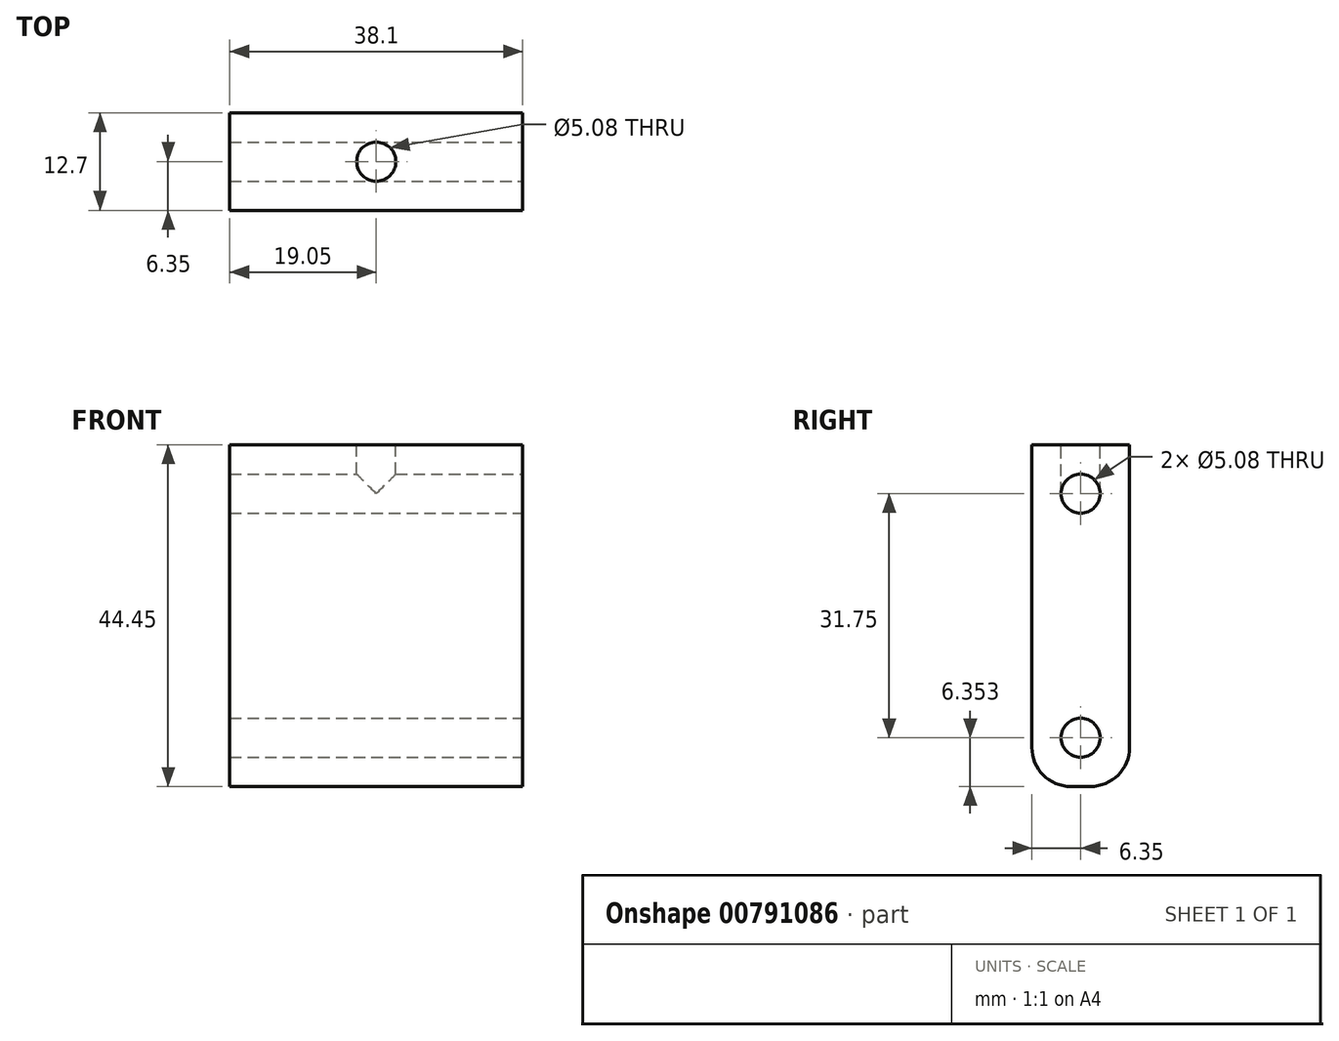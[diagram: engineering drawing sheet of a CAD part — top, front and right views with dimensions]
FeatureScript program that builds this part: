
annotation { "Feature Type Name" : "Feature", "Feature Type Description" : "" }
export const myFeature = defineFeature(function(context is Context, id is Id, definition is map)
    precondition{}
    {
        {
            var Q0;
            Q0=qCreatedBy(makeId("Front.planeOp"),FACE);
            var sketch = newSketch(context, id + "F0", { "sketchPlane" : qUnion([Q0])});
            skLineSegment(sketch, "E0.bottom", {"start": v(-38.1, 27.55) * mm, "end": v(0, 27.55) * mm});
            skLineSegment(sketch, "E0.top", {"start": v(-38.1, -16.9) * mm, "end": v(0, -16.9) * mm});
            skLineSegment(sketch, "E0.left", {"start": v(-38.1, 27.55) * mm, "end": v(-38.1, -16.9) * mm});
            skLineSegment(sketch, "E0.right", {"start": v(0, 27.55) * mm, "end": v(0, -16.9) * mm});
            skSolve(sketch);
        }
        {
            var Q0;
            Q0=qSketchRegion(id+"F0",true);
            extrude(context, id + "F1", {"entities" : qUnion([Q0]), "depth" : 12.7 * mm, "offsetDistance" : 25.4 * mm});
        }
        {
            var Q0;
            Q0=makeQuery(id+"F1.opExtrude","CAP_EDGE",EDGE,{"disambiguationData":[OSD([sQuery(id+"F0.wireOp",EDGE,"E0.top")])],"isStart":true});
            var Q1;
            Q1=makeQuery(id+"F1.opExtrude","CAP_EDGE",EDGE,{"disambiguationData":[OSD([sQuery(id+"F0.wireOp",EDGE,"E0.top")])],"isStart":false});
            fillet(context, id + "F2", {"entities" : qUnion([Q0, Q1]), "radius" : 5.08 * mm, "tangentPropagation" : true, "allowEdgeOverflow" : false});
        }
        {
            var Q0;
            Q0=makeQuery(id+"F1.opExtrude","SWEPT_FACE",FACE,{"disambiguationData":[OSD([sQuery(id+"F0.wireOp",EDGE,"E0.right")])]});
            var sketch = newSketch(context, id + "F3", { "sketchPlane" : qUnion([Q0])});
            skCircle(sketch, "E1", {"center": v(-6.35, -10.55) * mm, "radius": 2.54 * mm});
            skCircle(sketch, "E2", {"center": v(-6.35, 21.2) * mm, "radius": 2.54 * mm});
            skSolve(sketch);
        }
        {
            var Q0;
            Q0=qSketchRegion(id+"F3",true);
            extrude(context, id + "F4", {"entities" : qUnion([Q0]), "operationType" : NewBodyOperationType.REMOVE, "oppositeDirection" : true, "depth" : 38.1 * mm, "offsetDistance" : 25.4 * mm});
        }
        {
            var Q0;
            Q0=makeQuery(id+"F1.opExtrude","SWEPT_FACE",FACE,{"disambiguationData":[OSD([sQuery(id+"F0.wireOp",EDGE,"E0.bottom")])]});
            var sketch = newSketch(context, id + "F5", { "sketchPlane" : qUnion([Q0])});
            skCircle(sketch, "E3", {"center": v(-19.05, -6.35) * mm, "radius": 2.54 * mm});
            skSolve(sketch);
        }
        {
            var Q0;
            Q0=makeQuery(id+"F5.imprint","IMPRINT",FACE,{"disambiguationData":[TD([[makeQuery(id+"F5.imprint","IMPRINT",EDGE,{"derivedFrom":sQuery(id+"F5.wireOp",EDGE,"E3")}),1.0]])]});
            extrude(context, id + "F6", {"entities" : qUnion([Q0]), "operationType" : NewBodyOperationType.REMOVE, "oppositeDirection" : true, "depth" : 6.35 * mm, "offsetDistance" : 25.4 * mm});
        }
    });
